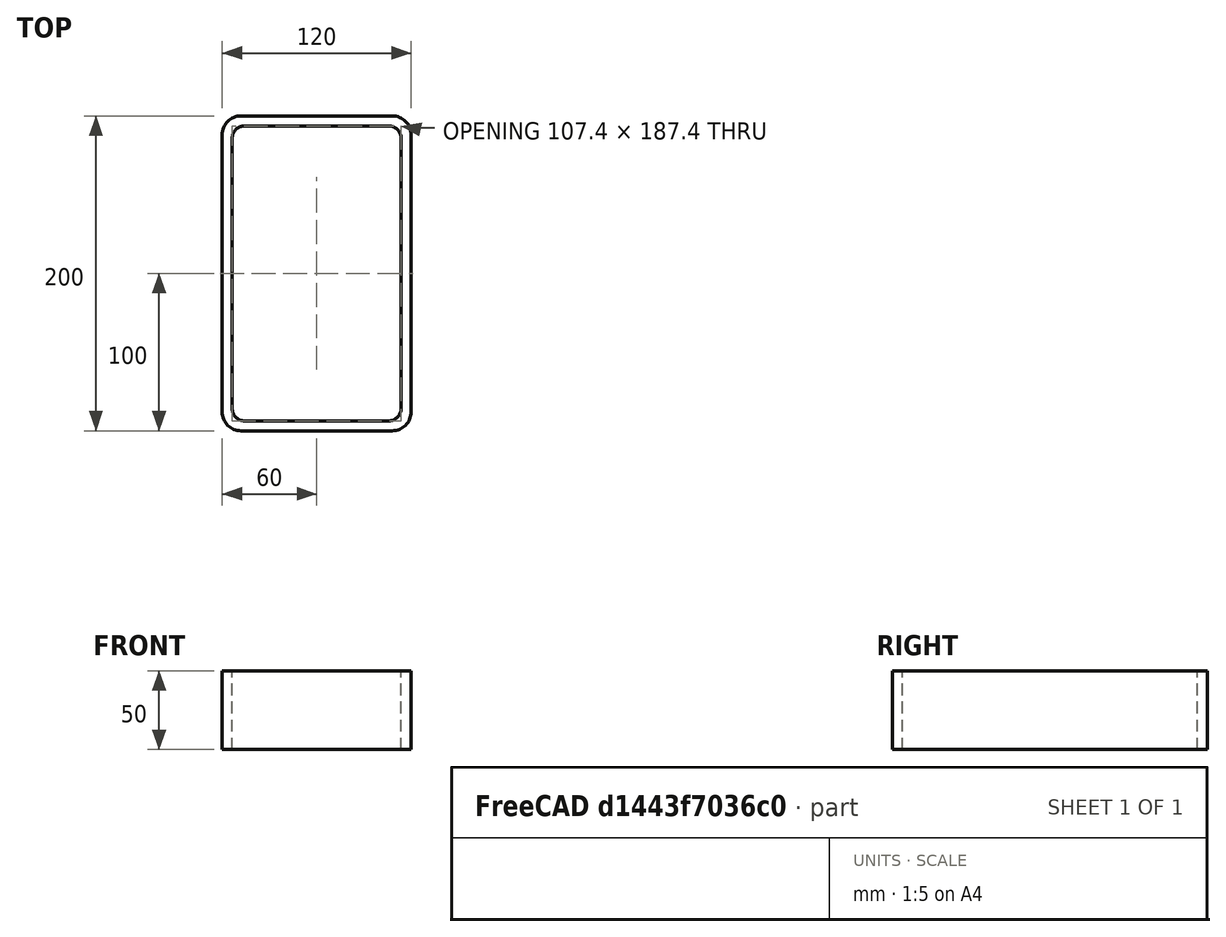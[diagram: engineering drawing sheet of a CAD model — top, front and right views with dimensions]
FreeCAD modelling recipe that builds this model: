
FCSTD DOCUMENT  (FreeCAD 0.15R4671 (Git))
Label: Rectangular hollow section 200x120x6.3 EN10219 S235JRH
License: All rights reserved
LicenseURL: http://en.wikipedia.org/wiki/All_rights_reserved
objects: Sketcher::SketchObject×1, Part::Extrusion×1
note: 2 computed .brp shape members not serialized (recipe doc carries the construction recipe); baked Part::Feature solids carry a one-line shape summary decoded from their .brp

FEATURE [Sketcher::SketchObject] Sketch
  sketch-geometry (16):
    g0: LineSegment StartX=-45.7 StartY=93.7 StartZ=0 EndX=45.7 EndY=93.7 EndZ=0
    g1: LineSegment StartX=53.7 StartY=85.7 StartZ=0 EndX=53.7 EndY=-85.7 EndZ=0
    g2: LineSegment StartX=45.7 StartY=-93.7 StartZ=0 EndX=-45.7 EndY=-93.7 EndZ=0
    g3: LineSegment StartX=-53.7 StartY=-85.7 StartZ=0 EndX=-53.7 EndY=85.7 EndZ=0
    g4: LineSegment StartX=-48 StartY=100 StartZ=0 EndX=48 EndY=100 EndZ=0
    g5: LineSegment StartX=60 StartY=88 StartZ=0 EndX=60 EndY=-88 EndZ=0
    g6: LineSegment StartX=48 StartY=-100 StartZ=0 EndX=-48 EndY=-100 EndZ=0
    g7: LineSegment StartX=-60 StartY=-88 StartZ=0 EndX=-60 EndY=88 EndZ=0
    g8: ArcOfCircle CenterX=-45.7 CenterY=85.7 CenterZ=0 NormalX=0 NormalY=0 NormalZ=1 Radius=8 StartAngle=1.5708 EndAngle=3.14159
    g9: ArcOfCircle CenterX=45.7 CenterY=85.7 CenterZ=0 NormalX=0 NormalY=0 NormalZ=1 Radius=8 StartAngle=0 EndAngle=1.5708
    g10: ArcOfCircle CenterX=45.7 CenterY=-85.7 CenterZ=0 NormalX=0 NormalY=0 NormalZ=1 Radius=8 StartAngle=4.71239 EndAngle=6.28319
    g11: ArcOfCircle CenterX=-45.7 CenterY=-85.7 CenterZ=0 NormalX=0 NormalY=0 NormalZ=1 Radius=8 StartAngle=3.14159 EndAngle=4.71239
    g12: ArcOfCircle CenterX=48 CenterY=88 CenterZ=0 NormalX=0 NormalY=0 NormalZ=1 Radius=12 StartAngle=0 EndAngle=1.5708
    g13: ArcOfCircle CenterX=48 CenterY=-88 CenterZ=0 NormalX=0 NormalY=0 NormalZ=1 Radius=12 StartAngle=4.71239 EndAngle=6.28319
    g14: ArcOfCircle CenterX=-48 CenterY=-88 CenterZ=0 NormalX=0 NormalY=0 NormalZ=1 Radius=12 StartAngle=3.14159 EndAngle=4.71239
    g15: ArcOfCircle CenterX=-48 CenterY=88 CenterZ=0 NormalX=0 NormalY=0 NormalZ=1 Radius=12 StartAngle=1.5708 EndAngle=3.14159
  constraints (36):
    c: Horizontal(g2)
    c: Vertical(g3)
    c: Horizontal(g6)
    c: Vertical(g7)
    c: Tangent(g3,g8) = 1.5708
    c: Tangent(g0,g8) = 1.5708
    c: Tangent(g0,g9) = 1.5708
    c: Tangent(g1,g9) = 1.5708
    c: Tangent(g1,g10) = 1.5708
    c: Tangent(g2,g10) = 1.5708
    c: Tangent(g2,g11) = 1.5708
    c: Tangent(g3,g11) = 1.5708
    c: Tangent(g4,g12) = 1.5708
    c: Tangent(g5,g12) = 1.5708
    c: Tangent(g5,g13) = 1.5708
    c: Tangent(g6,g13) = 1.5708
    c: Tangent(g6,g14) = 1.5708
    c: Tangent(g7,g14) = 1.5708
    c: Tangent(g7,g15) = 1.5708
    c: Tangent(g4,g15) = 1.5708
    c: Equal(g9,g8)
    c: Equal(g9,g11)
    c: Equal(g9,g10)
    c: Equal(g12,g15)
    c: Equal(g12,g14)
    c: Equal(g12,g13)
    c: Symmetric(g4,g6,g-1)
    c: Symmetric(g7,g5,g-2)
    c: DistanceY(g4,g6) = -200
    c: DistanceX(g7,g5) = 120
    c: Symmetric(g3,g1,g-2)
    c: Symmetric(g0,g2,g-1)
    c: DistanceY(g0,g4) = 6.3
    c: DistanceX(g5,g1) = -6.3
    c: Radius(g9) = 8
    c: Radius(g12) = 12
FEATURE [Part::Extrusion] Extrude  label="Rectangular hollow section 200x120x6.3 EN10219 S235JRH"
  Base = -> Sketch
  Dir = (0,0,50)
  Solid = true
